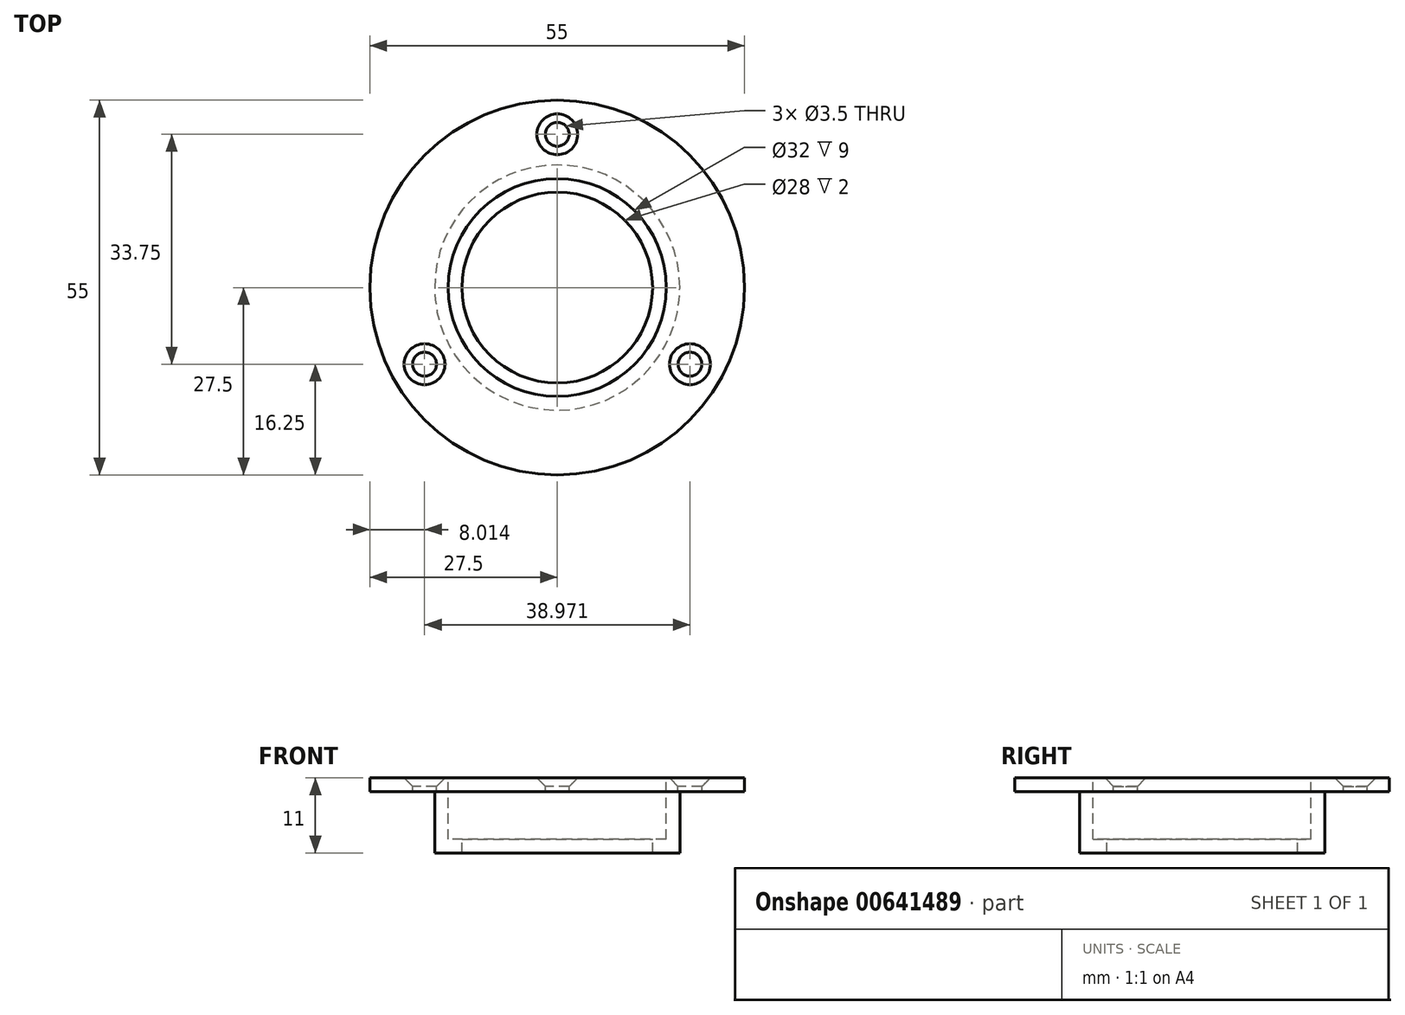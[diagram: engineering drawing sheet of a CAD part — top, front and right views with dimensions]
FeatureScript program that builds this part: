
annotation { "Feature Type Name" : "Feature", "Feature Type Description" : "" }
export const myFeature = defineFeature(function(context is Context, id is Id, definition is map)
    precondition{}
    {
        {
            var Q0;
            Q0=qCreatedBy(makeId("Top.planeOp"),FACE);
            var sketch = newSketch(context, id + "F0", { "sketchPlane" : qUnion([Q0])});
            skCircle(sketch, "E0", {"center": v(0, 0) * mm, "radius": 16 * mm});
            skCircle(sketch, "E1.0", {"center": v(0, 0) * mm, "radius": 18 * mm});
            skSolve(sketch);
        }
        {
            var Q0;
            Q0=makeQuery(id+"F0.imprint","IMPRINT",FACE,{"disambiguationData":[TD([[makeQuery(id+"F0.imprint","IMPRINT",EDGE,{"derivedFrom":sQuery(id+"F0.wireOp",EDGE,"E0")}),-1.0]])]});
            extrude(context, id + "F1", {"entities" : qUnion([Q0]), "depth" : -7 * mm, "offsetDistance" : 25 * mm});
        }
        {
            var Q0;
            Q0=qCreatedBy(makeId("Top.planeOp"),FACE);
            var sketch = newSketch(context, id + "F2", { "sketchPlane" : qUnion([Q0])});
            skCircle(sketch, "E2", {"center": v(0, 0) * mm, "radius": 16 * mm});
            skCircle(sketch, "E3", {"center": v(0, 0) * mm, "radius": 27.5 * mm});
            skSolve(sketch);
        }
        {
            var Q0;
            Q0 = qSketchRegion(id + "F2", true);
            extrude(context, id + "F3", {"entities" : qUnion([Q0]), "operationType" : NewBodyOperationType.ADD, "depth" : 2 * mm, "offsetDistance" : 25 * mm});
        }
        {
            var Q0;
            Q0=makeQuery(id+"F1.opExtrude","CAP_FACE",FACE,{"disambiguationData":[OSD([sQuery(id+"F0.wireOp",EDGE,"E0"),sQuery(id+"F0.wireOp",EDGE,"E1.0")])],"isStart":false});
            var sketch = newSketch(context, id + "F4", { "sketchPlane" : qUnion([Q0])});
            skCircle(sketch, "E4", {"center": v(0, 0) * mm, "radius": 18 * mm});
            skCircle(sketch, "E5", {"center": v(0, 0) * mm, "radius": 14 * mm});
            skSolve(sketch);
        }
        {
            var Q0;
            Q0 = qSketchRegion(id + "F4", true);
            extrude(context, id + "F5", {"entities" : qUnion([Q0]), "operationType" : NewBodyOperationType.ADD, "depth" : 2 * mm, "offsetDistance" : 25 * mm});
        }
        {
            var Q0;
            Q0=makeQuery(id+"F3.opExtrude","CAP_FACE",FACE,{"disambiguationData":[OSD([sQuery(id+"F2.wireOp",EDGE,"E2"),sQuery(id+"F2.wireOp",EDGE,"E3")])],"isStart":false});
            var sketch = newSketch(context, id + "F6", { "sketchPlane" : qUnion([Q0])});
            skCircle(sketch, "E6", {"center": v(0, 0) * mm, "radius": 22.5 * mm});
            skCircle(sketch, "E7", {"center": v(0, 22.5) * mm, "radius": 1.75 * mm});
            skCircle(sketch, "E8.1.0", {"center": v(-19.49, -11.25) * mm, "radius": 1.75 * mm});
            skCircle(sketch, "E8.2.0", {"center": v(19.49, -11.25) * mm, "radius": 1.75 * mm});
            skSolve(sketch);
        }
        {
            var Q0;
            Q0=sQuery(id+"F6.wireOp",VERTEX,"E7.center");
            var Q1;
            Q1=sQuery(id+"F6.wireOp",VERTEX,"E8.1.0.center");
            var Q2;
            Q2=sQuery(id+"F6.wireOp",VERTEX,"E8.2.0.center");
            var Q3;
            Q3=makeQuery(id+"F1.opExtrude","SWEPT_BODY",BODY,{"disambiguationData":[OSD([sQuery(id+"F0.wireOp",EDGE,"E0"),sQuery(id+"F0.wireOp",EDGE,"E1.0")])]});
            hole(context, id + "F7", {"style" : HoleStyle.C_SINK, "endStyle" : HoleEndStyle.THROUGH, "holeDiameter" : 3.5 * mm, "cSinkDiameter" : 6 * mm, "cSinkAngle" : 90 * degree, "majorDiameter" : 5 * mm, "isTappedThrough" : true, "tappedDepth" : 12 * mm, "tapClearance" : 3, "locations" : qUnion([Q0, Q1, Q2]), "scope" : qUnion([Q3])});
        }
    });
